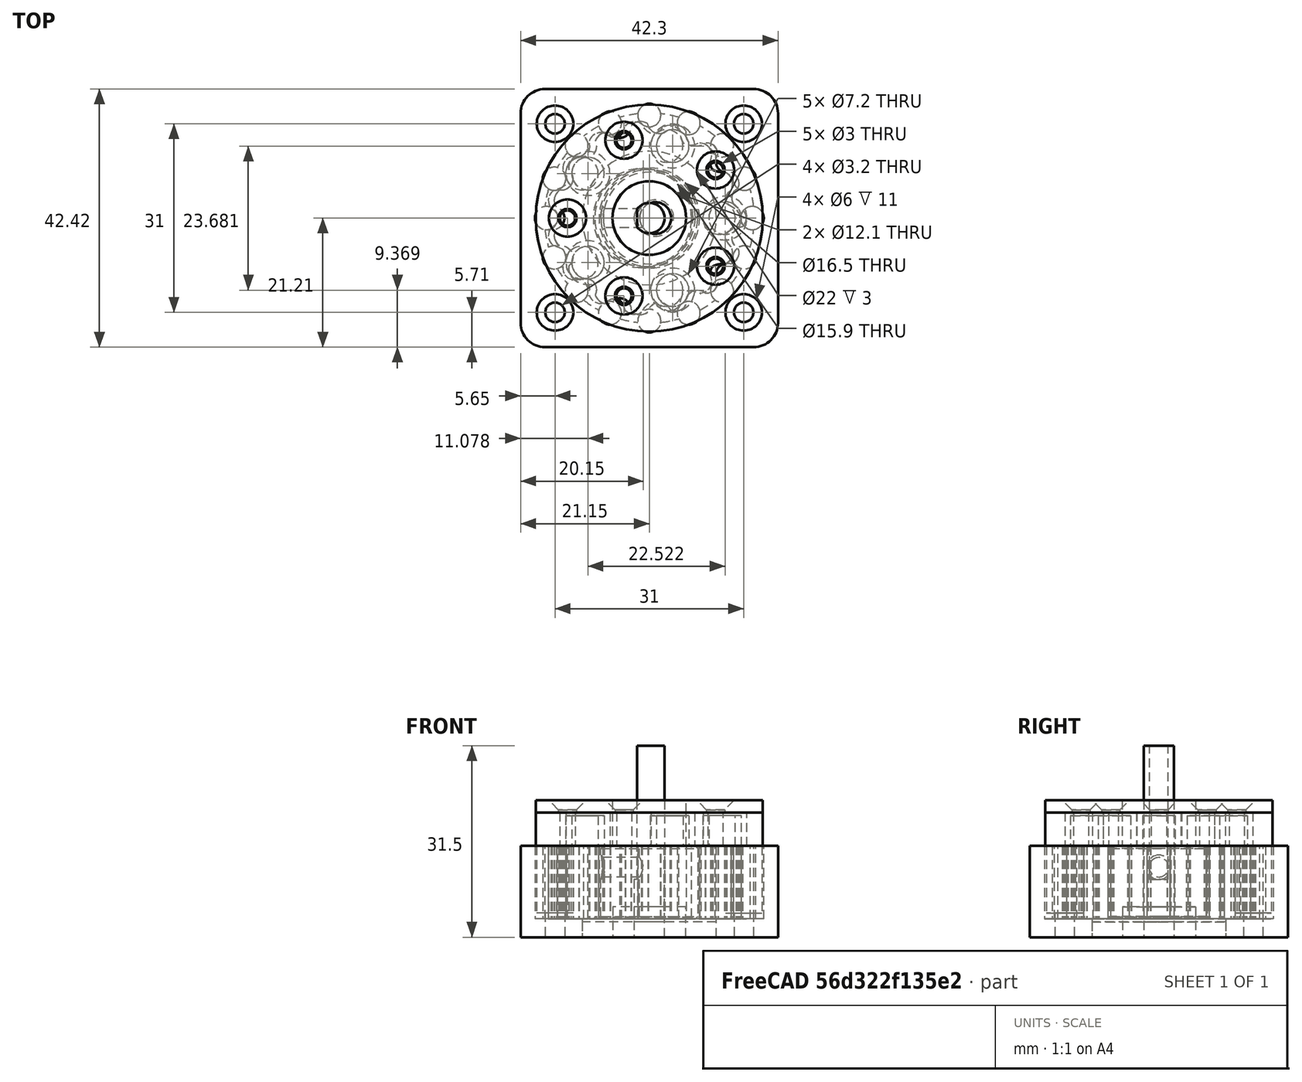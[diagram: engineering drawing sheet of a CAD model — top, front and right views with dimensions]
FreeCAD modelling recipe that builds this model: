
FCSTD DOCUMENT  (FreeCAD 0.21R31391 (Git))
Label: GearboxCycloidal
License: All rights reserved
LicenseURL: http://en.wikipedia.org/wiki/All_rights_reserved
objects: Sketcher::SketchObject×16, PartDesign::Pad×10, PartDesign::Body×9, App::Part×9, PartDesign::PolarPattern×4, TechDraw::DrawViewDimension×4, PartDesign::Pocket×3, PartDesign::FeaturePython×3, PartDesign::Hole×2, PartDesign::Mirrored×2, PartDesign::Chamfer×2, TechDraw::DrawViewPart×2, Spreadsheet::Sheet×1, PartDesign::Boolean×1, PartDesign::MultiTransform×1, Part::Feature×1, TechDraw::DrawSVGTemplate×1, TechDraw::DrawPage×1
note: 71 computed .brp shape members not serialized (recipe doc carries the construction recipe); baked Part::Feature solids carry a one-line shape summary decoded from their .brp

FEATURE [Spreadsheet::Sheet] Spreadsheet  label="SpreadSheet"
  cells = A2=Stepper; C2=Defaults; D2=enter negative numbers as =-0.5, not as -0.5; A3=StepperSize; B3(StepperSize)=42.3; A4=StepperShaftDiameter; B4(StepperShaftDiameter)=5; G4=Todo; A5=StepperShaftFlatLength; B5(StepperShaftFlatLength)=15; A6=StepperShaftFlatDepth; B6(StepperShaftFlatDepth)=0.5; A7=StepperShaftLength; B7(StepperShaftLength)=22; A8=StepperBoltHolediameter; B8(StepperBoltHolediameter)=3.2; A9=StepperRegisterDiameter; B9(StepperRegisterDiameter)=22; A10=StepperRegisterDepth; B10(StepperRegisterDepth)=2.5; A11=StepperBoltDistance; B11(StepperBoltDistance)=31; A12=StepperBodyCornerRadius; B12(StepperBodyCornerRadius)=4; A13=StepperShaftRotation; B13(StepperShaftRotation)=90; A15=GearBox; A16=GearBoxBaseThickness; B16(GearBoxBaseThickness)=0.5; D16=The gearbox bottom thickness above the the stepper register; A17=GearBoxBottomPosition; B17(GearBoxBottomPosition)==GearBoxBaseThickness + StepperRegisterDepth; D17=The heigth from the stepper flange to the gearbox bottom; A18=GearBoxGearPocketDiameter; B18(GearBoxGearPocketDiameter)=34.5; D18=The pocket for the cycloidal gear; A19=GearBoxRollerTopPosition; B19(GearBoxRollerTopPosition)==GearBoxBottomPosition + GearThickness; A20=GearBoxBoltHeadDiameter; B20(GearBoxBoltHeadDiameter)=6; A21=GearBoxBoltHeadDepth; B21(GearBoxBoltHeadDepth)==GearBoxRollerTopPosition - 4; A23=Cycloid Gear; A24=PinCircleRadiusCorrected; B24==PinCircleRadiusCorrection + PinCircleRadius; A25=PinCircleRadius; B25(PinCircleRadius)=16.9; C25=17; D25=The radius of the outside rollers; A26=PinCircleRadiusCorrection; B26(PinCircleRadiusCorrection)==-0.09; C26==-0.05; D26=3D printing correction for gear disk only, must be0 or lager than 0.1, otherwise error in gear calculation; A27=GearHoleRadius; B27(GearHoleRadius)=8; D27=The radius of the eccenter hole; A28=GearHoleRadiusCorrection; B28(GearHoleRadiusCorrection)==-0.05; D28=3D printing correction for gear disk only; A29=Eccentricity; B29(Eccentricity)=1; C29=1; D29=eccentricity of the eccenter; A30=GearThickness; B30(GearThickness)=12; C30=11; A31=RollerRotation; B31(RollerRotation)=0; C31=36; D31=To prevent the screw hole in the roller; A32=RollerDiameter; B32(RollerDiameter)=3.8; C32=5; A33=TeethNumber; B33(TeethNumber)=15; C33=10; D33=The number of teeth of the gear, defines the reduction; A35=GearCamDiameter; B35(GearCamDiameter)=5; D35=Diameter of the cam (shaft) to drive the shaft.; A36=GearCamDiameterCorrection; B36(GearCamDiameterCorrection)=0.35; A37=GearCamRadius; B37(GearCamRadius)==(GearHoleRadius + PinCircleRadius) / 2; C37=12.5; D37=The radius at witch the cams are placed; A38=GearCamThickness; B38(GearCamThickness)=5; C38=5; D38=The higth of the gear cams; A39=GearCamCount; B39(GearCamCount)=5; C39=5; D39=The number of gear cams; A40=SegementCount; B40(SegementCount)=16; C40=80; D40=High values are more precise. At higher roller counts, this results in errors; A42=Ecccenter; A43=EccenterOuterDiameter; B43(EccenterOuterDiameter)==GearHoleRadius * 2; C43=16; D43=The outer diameter of the eccenter; A44=EccenterOuterDiameterCorrection; B44(EccenterOuterDiameterCorrection)==0 - 0.1; C44=-0,1; D44=Correction for 3D print; A45=EccenterShaftHoleDiameter; B45(EccenterShaftHoleDiameter)==StepperShaftDiameter; C45=5; D45=The hole for the stepper shaft; A46=EccenterShaftHoleDiameterCorrection; B46(EccenterShaftHoleDiameterCorrection)=0.2; C46=0.2; D46=Correction for 3D print; A47=EccenterScrewHoleHeight; B47(EccenterScrewHoleHeight)=8.5; C47=8.5; D47=The position of the scres must be at the flat portion of the shaft; A48=EccenterScrewHoleDiameter; B48(EccenterScrewHoleDiameter)=3.2; C48=M4  3.2 mm; D48=The hole to tap the thread ; A49=EccenterRotation; B49(EccenterRotation)=90; C49=90; D49=To position the eccenter visual, just cosmetic ; A50=EccenterHeigth; B50(EccenterHeigth)==GearThickness; D50=The heigth of the eccenter; A52=OutputShaft; A53=OutputShaftDiameter; B53(OutputShaftDiameter)==StepperSize - 5; A54=OutputShaftThickNess; B54(OutputShaftThickNess)==GearCamThickness + 0.5; A55=PillarDiameterCorrection; B55(PillarDiameterCorrection)=-0.2; A56=OutputShaftCamHoleDiameter; B56(OutputShaftCamHoleDiameter)==GearCamDiameter + Eccentricity * 2; A57=OutputShaftCamHoleDiameterCorection; B57(OutputShaftCamHoleDiameterCorection)=0.2; A58=OutputShaftBoltDistance; B58(OutputShaftBoltDistance)==GearCamRadius + GearCamDiameter - 4; A59=OutputShaftBoltThreadDiameter; B59(OutputShaftBoltThreadDiameter)=2.5; A60=OutputShaftBoltDiameter; B60(OutputShaftBoltDiameter)=3; A61=OutputShaftTopPosition; B61(OutputShaftTopPosition)==GearBoxRollerTopPosition + OutputShaftThickNess; A62=OutputShaftHoleRotation; B62(OutputShaftHoleRotation)==90 - 360 / B53; A63=OutputShaftBearingOuterDiameterCorrection; B63(OutputShaftBearingOuterDiameterCorrection)=0.1; D63=Correction for 3D print; A65=GearMountingPlate; A66=GearMountingPlateThickness; B66(GearMountingPlateThickness)=2; A67=GearMountingPlateTopPosition; B67(GearMountingPlateTopPosition)==OutputShaftTopPosition + GearMountingPlateThickness; A68=GearMountingPlateDiameter; B68(GearMountingPlateDiameter)==OutputShaftDiameter; A69=GearMountingPlateBearingOuterDiameterCorrection; B69(GearMountingPlateBearingOuterDiameterCorrection)==OutputShaftBearingOuterDiameterCorrection; C69=0.1; D69=Correction for 3D print; A71=OutputGear; A72=OutputGearThickness; B72(OutputGearThickness)=6; A73=OutputGearTeeth; B73(OutputGearTeeth)=17; A74=OutputGearTopPosition; B74(OutputGearTopPosition)==OutputShaftTopPosition + OutputGearThickness; A75=OutputGearBearingPocketDepth; B75(OutputGearBearingPocketDepth)==BearingThickness - GearMountingPlateThickness; A76=OutputGearBearingOuterDiameterCorrection; B76(OutputGearBearingOuterDiameterCorrection)==OutputShaftBearingOuterDiameterCorrection; C76=0.1; D76=correction for 3D print; A78=Bearing; A79=BearingOuterDiameter; B79(BearingOuterDiameter)=12; A80=BearingInnerDiameter; B80(BearingInnerDiameter)=5; A81=BearingThickness; B81(BearingThickness)=5; A82=BearingTotalLength; B82==OutputGearTopPosition - GearBoxRollerTopPosition
FEATURE [Sketcher::SketchObject] Sketch026
  FullyConstrained = false
  MapMode = 5
  Support = -> [XY_Plane020]
  expr: Constraints[23] = Spreadsheet.StepperBodyCornerRadius
  expr: Constraints[27] = Spreadsheet.StepperRegisterDiameter
  expr: Constraints[5] = Spreadsheet.StepperSize
  sketch-geometry (13):
    g0: Circle CenterX=0 CenterY=0 CenterZ=0 NormalX=0 NormalY=0 NormalZ=1 AngleXU=0 Radius=11
    g1: LineSegment StartX=-17.15 StartY=21.2137 StartZ=0 EndX=17.15 EndY=21.2137 EndZ=0
    g2: LineSegment StartX=21.15 StartY=17.2137 StartZ=0 EndX=21.15 EndY=-17.2137 EndZ=0
    g3: LineSegment StartX=17.15 StartY=-21.2137 StartZ=0 EndX=-17.15 EndY=-21.2137 EndZ=0
    g4: LineSegment StartX=-21.15 StartY=-17.2137 StartZ=0 EndX=-21.15 EndY=17.2137 EndZ=0
    g5: ArcOfCircle CenterX=-17.15 CenterY=17.2137 CenterZ=0 NormalX=0 NormalY=0 NormalZ=1 AngleXU=0 Radius=4 StartAngle=1.5708 EndAngle=3.14159
    g6: GeomPoint X=-21.15 Y=21.2137 Z=0
    g7: ArcOfCircle CenterX=17.15 CenterY=17.2137 CenterZ=0 NormalX=0 NormalY=0 NormalZ=1 AngleXU=0 Radius=4 StartAngle=-9e-16 EndAngle=1.5708
    g8: GeomPoint X=21.15 Y=21.2137 Z=0
    g9: ArcOfCircle CenterX=-17.15 CenterY=-17.2137 CenterZ=0 NormalX=0 NormalY=0 NormalZ=1 AngleXU=0 Radius=4 StartAngle=3.14159 EndAngle=4.71239
    g10: GeomPoint X=-21.15 Y=-21.2137 Z=0
    g11: ArcOfCircle CenterX=17.15 CenterY=-17.2137 CenterZ=0 NormalX=0 NormalY=0 NormalZ=1 AngleXU=0 Radius=4 StartAngle=4.71239 EndAngle=6.28319
    g12: GeomPoint X=21.15 Y=-21.2137 Z=0
  constraints (28):
    c: Coincident(g0,g-1)
    c: Horizontal(g1)
    c: Horizontal(g3)
    c: Vertical(g2)
    c: Vertical(g4)
    c: DistanceX(g6,g8) = 42.3
    c: Symmetric(g10,g8,g0)
    c: PointOnObject(g6,g1)
    c: PointOnObject(g6,g4)
    c: Tangent(g1,g5) = 1.5708
    c: Tangent(g4,g5) = 1.5708
    c: PointOnObject(g8,g1)
    c: PointOnObject(g8,g2)
    c: Tangent(g1,g7) = 1.5708
    c: Tangent(g2,g7) = 1.5708
    c: PointOnObject(g10,g4)
    c: PointOnObject(g10,g3)
    c: Tangent(g4,g9) = 1.5708
    c: Tangent(g3,g9) = 1.5708
    c: PointOnObject(g12,g3)
    c: PointOnObject(g12,g2)
    c: Tangent(g3,g11) = 1.5708
    c: Tangent(g2,g11) = 1.5708
    c: Radius(g5) = 4
    c: Equal(g5,g7)
    c: Equal(g7,g11)
    c: Equal(g11,g9)
    c: Diameter(g0) = 22
FEATURE [PartDesign::Pad] Pad005
  Direction = (0,0,1)
  Length = 15
  Length2 = 10
  Profile = -> Sketch026
  ReferenceAxis = -> Sketch026 [N_Axis]
  Type = 0
  expr: Length = Spreadsheet.GearBoxRollerTopPosition
FEATURE [Sketcher::SketchObject] Sketch028
  FullyConstrained = true
  MapMode = 11
  Placement = pos=(0,0,15) rot=(0,0,1;1.5708rad)
  Support = -> [Pad005]
  expr: Constraints[1] = Spreadsheet.GearBoxGearPocketDiameter
  sketch-geometry (1):
    g0: Circle CenterX=0 CenterY=0 CenterZ=0 NormalX=0 NormalY=0 NormalZ=1 AngleXU=0 Radius=17.25
  constraints (2):
    c: Coincident(g0,g-1)
    c: Diameter(g0) = 34.5
FEATURE [PartDesign::Pocket] Pocket007
  BaseFeature = -> Pad005
  Direction = (0,0,-1)
  Length = 12
  Length2 = 5
  Profile = -> Sketch028
  ReferenceAxis = -> Sketch028 [N_Axis]
  Type = 0
  expr: Length = Spreadsheet.GearThickness
FEATURE [PartDesign::FeaturePython] hypocycloidgear003  label="HypoCycloidGearRollers"  # WARN: FeaturePython — macro-defined, semantics opaque (R4)
  AttacherType = Attacher::AttachEngine3D
  Placement = pos=(0,0,9) rot=(0,0,1;0rad)
  center_pins = true
  disk_height = 11.9
  eccentricity = 1
  hole_radius = 8
  pin_circle_radius = 16.9
  pin_height = 12
  pressure_angle_lim = 50
  pressure_angle_offset = 0.01
  roller_diameter = 3.8
  segment_count = 16
  show_disk0 = false
  show_disk1 = false
  show_pins = true
  teeth_number = 15
  version = 0.0.3
  expr: .Placement.Base.z = Spreadsheet.GearBoxBottomPosition + Spreadsheet.GearThickness / 2
  expr: .Placement.Rotation.Angle = Spreadsheet.RollerRotation
  expr: disk_height = Spreadsheet.GearThickness - 0.1
  expr: eccentricity = Spreadsheet.Eccentricity
  expr: hole_radius = Spreadsheet.GearHoleRadius
  expr: pin_circle_radius = Spreadsheet.PinCircleRadius
  expr: pin_height = Spreadsheet.GearThickness
  expr: roller_diameter = Spreadsheet.RollerDiameter
  expr: segment_count = Spreadsheet.SegementCount
  expr: teeth_number = Spreadsheet.TeethNumber
FEATURE [PartDesign::Body] Body006  label="HypoCycloidGearRollersBody"
  Group = -> [hypocycloidgear003]
  Origin = -> Origin021
  Tip = -> hypocycloidgear003
FEATURE [PartDesign::Boolean] Boolean
  BaseFeature = -> Pocket007
  Group = -> [Body006]
  Type = 0
FEATURE [Sketcher::SketchObject] Sketch029
  FullyConstrained = false
  MapMode = 5
  Placement = pos=(0,0,15) rot=(0,0,1;0rad)
  Support = -> [Boolean]
  expr: Constraints[10] = Spreadsheet.StepperBoltDistance
  expr: Constraints[11] = Spreadsheet.StepperBoltHolediameter
  sketch-geometry (5):
    g0: Circle CenterX=-15.5 CenterY=15.5 CenterZ=0 NormalX=0 NormalY=0 NormalZ=1 AngleXU=0 Radius=1.6
    g1: LineSegment StartX=-15.5 StartY=15.5 StartZ=0 EndX=15.5 EndY=15.5 EndZ=0
    g2: LineSegment StartX=15.5 StartY=15.5 StartZ=0 EndX=15.5 EndY=-15.5 EndZ=0
    g3: LineSegment StartX=15.5 StartY=-15.5 StartZ=0 EndX=-15.5 EndY=-15.5 EndZ=0
    g4: LineSegment StartX=-15.5 StartY=-15.5 StartZ=0 EndX=-15.5 EndY=15.5 EndZ=0
  constraints (12):
    c: Coincident(g1,g2)
    c: Coincident(g2,g3)
    c: Coincident(g3,g4)
    c: Coincident(g4,g1)
    c: Horizontal(g1)
    c: Horizontal(g3)
    c: Vertical(g2)
    c: Vertical(g4)
    c: Equal(g4,g1)
    c: Symmetric(g3,g1,g-1)
    c: DistanceX(g1,g1) = 31
    c: Diameter(g0) = 3.2
FEATURE [PartDesign::Hole] Hole
  BaseFeature = -> Boolean
  CustomThreadClearance = 0
  Depth = 124.756
  DepthType = 1
  Diameter = 3.2
  DrillForDepth = false
  DrillPoint = 1
  DrillPointAngle = 118
  HoleCutCountersinkAngle = 90
  HoleCutCustomValues = false
  HoleCutDepth = 11
  HoleCutDiameter = 6
  HoleCutType = 1
  ModelThread = false
  Profile = -> Sketch029
  Tapered = false
  TaperedAngle = 90
  ThreadClass = 0
  ThreadDepth = 124.756
  ThreadDepthType = 0
  ThreadDirection = 0
  ThreadFit = 0
  ThreadSize = 0
  ThreadType = 0
  Threaded = false
  UseCustomThreadClearance = false
  expr: Diameter = Spreadsheet.StepperBoltHolediameter
  expr: HoleCutDepth = Spreadsheet.GearBoxBoltHeadDepth
  expr: HoleCutDiameter = Spreadsheet.GearBoxBoltHeadDiameter
FEATURE [PartDesign::Mirrored] Mirrored
  MirrorPlane = -> Sketch029 [V_Axis]
FEATURE [PartDesign::Mirrored] Mirrored001
  MirrorPlane = -> XZ_Plane020
FEATURE [PartDesign::MultiTransform] MultiTransform
  BaseFeature = -> Hole
  Originals = -> [Hole]
  Transformations = -> [Mirrored,Mirrored001]
FEATURE [PartDesign::Body] Body005  label="NemaBaseBody"
  Group = -> [Sketch026,Pad005,Sketch028,Pocket007,Boolean,Sketch029,Hole,MultiTransform,Mirrored,Mirrored001]
  Origin = -> Origin020
  Tip = -> MultiTransform
FEATURE [App::Part] Part005  label="NemaBase"
  Group = -> [Body005]
  Origin = -> Origin019
FEATURE [PartDesign::FeaturePython] hypocycloidgear004  label="HypoCycloidGearDisk001"  # WARN: FeaturePython — macro-defined, semantics opaque (R4)
  AttacherType = Attacher::AttachEngine3D
  Placement = pos=(1,0,3) rot=(0,0,1;0rad)
  center_pins = true
  disk_height = 12
  eccentricity = 1
  hole_radius = 7.95
  pin_circle_radius = 16.81
  pin_height = 12
  pressure_angle_lim = 50
  pressure_angle_offset = 0.01
  roller_diameter = 3.8
  segment_count = 16
  show_disk0 = true
  show_disk1 = false
  show_pins = false
  teeth_number = 15
  version = 0.0.3
  expr: .Placement.Base.x = Spreadsheet.Eccentricity
  expr: .Placement.Base.z = Spreadsheet.GearBoxBottomPosition
  expr: .Placement.Rotation.Angle = Spreadsheet.RollerRotation
  expr: disk_height = Spreadsheet.GearThickness
  expr: eccentricity = Spreadsheet.Eccentricity
  expr: hole_radius = Spreadsheet.GearHoleRadius + Spreadsheet.GearHoleRadiusCorrection
  expr: pin_circle_radius = Spreadsheet.PinCircleRadius + Spreadsheet.PinCircleRadiusCorrection
  expr: pin_height = Spreadsheet.GearThickness
  expr: roller_diameter = Spreadsheet.RollerDiameter
  expr: segment_count = Spreadsheet.SegementCount
  expr: teeth_number = Spreadsheet.TeethNumber
FEATURE [Sketcher::SketchObject] Sketch035
  FullyConstrained = true
  MapMode = 5
  Support = -> [XY_Plane030]
  expr: Constraints[1] = Spreadsheet.StepperRegisterDiameter
  sketch-geometry (1):
    g0: Circle CenterX=0 CenterY=0 CenterZ=0 NormalX=0 NormalY=0 NormalZ=1 AngleXU=0 Radius=11
  constraints (2):
    c: Coincident(g0,g-1)
    c: Diameter(g0) = 22
FEATURE [PartDesign::Pad] Pad
  Direction = (0,0,1)
  Length = 2.5
  Length2 = 10
  Profile = -> Sketch035
  ReferenceAxis = -> Sketch035 [N_Axis]
  Type = 0
  expr: Length = Spreadsheet.StepperRegisterDepth
FEATURE [Sketcher::SketchObject] Sketch036
  FullyConstrained = true
  MapMode = 5
  Placement = pos=(0,0,2.5) rot=(0,0,1;0rad)
  Support = -> [Pad]
  expr: Constraints[1] = Spreadsheet.StepperShaftDiameter
  sketch-geometry (1):
    g0: Circle CenterX=0 CenterY=0 CenterZ=0 NormalX=0 NormalY=0 NormalZ=1 AngleXU=0 Radius=2.5
  constraints (2):
    c: Coincident(g0,g-1)
    c: Diameter(g0) = 5
FEATURE [PartDesign::Pad] Pad008
  BaseFeature = -> Pad
  Direction = (0,0,1)
  Length = 7
  Length2 = 10
  Profile = -> Sketch036
  ReferenceAxis = -> Sketch036 [N_Axis]
  Type = 0
  expr: Length = Spreadsheet.StepperShaftLength - Spreadsheet.StepperShaftFlatLength
FEATURE [Sketcher::SketchObject] Sketch037
  AttachmentOffset = pos=(0,0,0) rot=(0,0,1;1.5708rad)
  FullyConstrained = false
  MapMode = 5
  Placement = pos=(0,0,9.5) rot=(0,0,1;1.5708rad)
  Support = -> [Pad008]
  expr: .AttachmentOffset.Rotation.Angle = Spreadsheet.StepperShaftRotation
  expr: Constraints[2] = Spreadsheet.StepperShaftDiameter
  sketch-geometry (2):
    g0: ArcOfCircle CenterX=0 CenterY=0 CenterZ=0 NormalX=0 NormalY=0 NormalZ=1 AngleXU=0 Radius=2.5 StartAngle=2.2143 EndAngle=7.21048
    g1: LineSegment StartX=-1.5 StartY=2 StartZ=0 EndX=1.5 EndY=2 EndZ=0
  constraints (5):
    c: Coincident(g0,g-1)
    c: Horizontal(g1)
    c: Diameter(g0) = 5
    c: Coincident(g0,g1)
    c: Coincident(g0,g1)
FEATURE [PartDesign::Pad] Pad009
  BaseFeature = -> Pad008
  Direction = (0,0,1)
  Length = 22
  Length2 = 10
  Profile = -> Sketch037
  ReferenceAxis = -> Sketch037 [N_Axis]
  Type = 0
  expr: Length = Spreadsheet.StepperShaftLength
FEATURE [PartDesign::Body] Body008  label="ShaftBody"
  Group = -> [Sketch035,Pad,Sketch036,Pad008,Sketch037,Pad009]
  Origin = -> Origin030
  Tip = -> Pad009
FEATURE [App::Part] Part007  label="Shaft"
  Group = -> [Body008]
  Origin = -> Origin029
FEATURE [Sketcher::SketchObject] Sketch038
  FullyConstrained = true
  MapMode = 5
  Support = -> [XY_Plane032]
  expr: Constraints[1] = Spreadsheet.OutputShaftDiameter
  expr: Constraints[3] = Spreadsheet.BearingOuterDiameter + Spreadsheet.OutputShaftBearingOuterDiameterCorrection
  sketch-geometry (2):
    g0: Circle CenterX=0 CenterY=0 CenterZ=0 NormalX=0 NormalY=0 NormalZ=1 AngleXU=0 Radius=18.65
    g1: Circle CenterX=0 CenterY=0 CenterZ=0 NormalX=0 NormalY=0 NormalZ=1 AngleXU=0 Radius=6.05
  constraints (4):
    c: Coincident(g0,g-1)
    c: Diameter(g0) = 37.3
    c: Coincident(g1,g0)
    c: Diameter(g1) = 12.1
FEATURE [PartDesign::Pad] Pad010
  Direction = (0,0,1)
  Length = 5.5
  Length2 = 10
  Profile = -> Sketch038
  ReferenceAxis = -> Sketch038 [N_Axis]
  Type = 0
  expr: Length = Spreadsheet.OutputShaftThickNess
FEATURE [Sketcher::SketchObject] Sketch039
  FullyConstrained = true
  MapMode = 5
  expr: Constraints[0] = Spreadsheet.OutputShaftCamHoleDiameter + Spreadsheet.OutputShaftCamHoleDiameterCorection
  expr: Constraints[2] = Spreadsheet.GearCamRadius
  expr: Constraints[5] = 360 / Spreadsheet.GearCamCount / 2
  expr: Constraints[6] = Spreadsheet.OutputShaftBoltDistance
  expr: Constraints[7] = Spreadsheet.OutputShaftBoltThreadDiameter
  sketch-geometry (3):
    g0: Circle CenterX=12.45 CenterY=0 CenterZ=0 NormalX=0 NormalY=0 NormalZ=1 AngleXU=0 Radius=3.6
    g1: Circle CenterX=10.8813 CenterY=7.90571 CenterZ=0 NormalX=0 NormalY=0 NormalZ=1 AngleXU=0 Radius=1.25
    g2: LineSegment StartX=10.8813 StartY=7.90571 StartZ=0 EndX=0 EndY=0 EndZ=0
  constraints (8):
    c: Diameter(g0) = 7.2
    c: PointOnObject(g0,g-1)
    c: DistanceX(g-1,g0) = 12.45
    c: Coincident(g2,g1)
    c: Coincident(g2,g-1)
    c: Angle(g-1,g2) = 0.628319
    c: Distance(g2,g1) = 13.45
    c: Diameter(g1) = 2.5
FEATURE [PartDesign::Pocket] Pocket008
  BaseFeature = -> Pad010
  Direction = (0,0,-1)
  Length = 5
  Length2 = 5
  Profile = -> Sketch039
  ReferenceAxis = -> Sketch039 [N_Axis]
  Reversed = true
  Type = 1
FEATURE [PartDesign::PolarPattern] PolarPattern001
  Angle = 360
  Axis = -> Z_Axis032
  BaseFeature = -> Pocket008
  Occurrences = 5
  Originals = -> [Pocket008]
  expr: Occurrences = Spreadsheet.GearCamCount
FEATURE [PartDesign::Body] Body009  label="OutputShaftBody"
  Group = -> [Sketch038,Pad010,Sketch039,Pocket008,PolarPattern001]
  Origin = -> Origin032
  Placement = pos=(0,0,15) rot=(0,0,1;0rad)
  Tip = -> PolarPattern001
  expr: .Placement.Base.z = Spreadsheet.GearBoxRollerTopPosition
FEATURE [App::Part] Part008  label="OutputShaft"
  Group = -> [Body009]
  Origin = -> Origin031
FEATURE [Sketcher::SketchObject] Sketch041
  FullyConstrained = true
  MapMode = 5
  Support = -> [XY_Plane034]
  expr: Constraints[2] = Spreadsheet.BearingInnerDiameter
  expr: Constraints[3] = Spreadsheet.BearingOuterDiameter
  sketch-geometry (2):
    g0: Circle CenterX=0 CenterY=0 CenterZ=0 NormalX=0 NormalY=0 NormalZ=1 AngleXU=0 Radius=2.5
    g1: Circle CenterX=0 CenterY=0 CenterZ=0 NormalX=0 NormalY=0 NormalZ=1 AngleXU=0 Radius=6
  constraints (4):
    c: Coincident(g0,g-1)
    c: Coincident(g1,g0)
    c: Diameter(g0) = 5
    c: Diameter(g1) = 12
FEATURE [PartDesign::Pad] Pad011
  Direction = (0,0,1)
  Length = 5
  Length2 = 10
  Profile = -> Sketch041
  ReferenceAxis = -> Sketch041 [N_Axis]
  Type = 0
  expr: Length = Spreadsheet.BearingThickness
FEATURE [PartDesign::Body] Body010  label="Bearing11x5x5Body"
  Group = -> [Sketch041,Pad011]
  Origin = -> Origin034
  Tip = -> Pad011
FEATURE [App::Part] Part009  label="Bearing11x5x5"
  Group = -> [Body010]
  Origin = -> Origin033
  Placement = pos=(0,0,15) rot=(0,0,1;0rad)
  expr: .Placement.Base.z = Spreadsheet.GearBoxRollerTopPosition
FEATURE [Sketcher::SketchObject] Sketch046
  AttachmentOffset = pos=(0,0,20.5) rot=(0,0,1;0rad)
  FullyConstrained = true
  MapMode = 5
  Placement = pos=(0,0,20.5) rot=(0,0,1;0rad)
  Support = -> [XY_Plane041]
  expr: .AttachmentOffset.Base.z = Spreadsheet.OutputShaftTopPosition
  expr: Constraints[1] = Spreadsheet.GearMountingPlateDiameter
  expr: Constraints[3] = Spreadsheet.BearingOuterDiameter + Spreadsheet.GearMountingPlateBearingOuterDiameterCorrection
  sketch-geometry (2):
    g0: Circle CenterX=0 CenterY=0 CenterZ=0 NormalX=0 NormalY=0 NormalZ=1 AngleXU=0 Radius=18.65
    g1: Circle CenterX=0 CenterY=0 CenterZ=0 NormalX=0 NormalY=0 NormalZ=1 AngleXU=0 Radius=6.05
  constraints (4):
    c: Coincident(g0,g-1)
    c: Diameter(g0) = 37.3
    c: Coincident(g1,g0)
    c: Diameter(g1) = 12.1
FEATURE [PartDesign::Pad] Pad013
  Direction = (0,0,1)
  Length = 2
  Length2 = 10
  Profile = -> Sketch046
  ReferenceAxis = -> Sketch046 [N_Axis]
  Type = 0
  expr: Length = Spreadsheet.GearMountingPlateThickness
FEATURE [Sketcher::SketchObject] Sketch047
  FullyConstrained = true
  MapMode = 5
  Placement = pos=(0,0,22.5) rot=(0,0,1;0rad)
  Support = -> [Pad013]
  expr: Constraints[0] = Spreadsheet.OutputShaftBoltDistance
  expr: Constraints[1] = Spreadsheet.OutputShaftBoltThreadDiameter
  expr: Constraints[4] = 360 / Spreadsheet.GearCamCount / 2
  sketch-geometry (2):
    g0: Circle CenterX=10.8813 CenterY=7.90571 CenterZ=0 NormalX=0 NormalY=0 NormalZ=1 AngleXU=0 Radius=1.25
    g1: LineSegment StartX=10.8813 StartY=7.90571 StartZ=0 EndX=0 EndY=0 EndZ=0
  constraints (5):
    c: Distance(g-1,g0) = 13.45
    c: Diameter(g0) = 2.5
    c: Coincident(g1,g0)
    c: Coincident(g1,g-1)
    c: Angle(g-1,g1) = 0.628319
FEATURE [PartDesign::Hole] Hole001
  BaseFeature = -> Pad013
  CustomThreadClearance = 0
  Depth = 118.051
  DepthType = 1
  Diameter = 3
  DrillForDepth = false
  DrillPoint = 1
  DrillPointAngle = 118
  HoleCutCountersinkAngle = 90
  HoleCutCustomValues = false
  HoleCutDepth = 0
  HoleCutDiameter = 6.1
  HoleCutType = 2
  ModelThread = false
  Profile = -> Sketch047
  Tapered = false
  TaperedAngle = 90
  ThreadClass = 0
  ThreadDepth = 118.051
  ThreadDepthType = 0
  ThreadDirection = 0
  ThreadFit = 0
  ThreadSize = 0
  ThreadType = 0
  Threaded = false
  UseCustomThreadClearance = false
  expr: Diameter = Spreadsheet.OutputShaftBoltDiameter
FEATURE [PartDesign::PolarPattern] PolarPattern002
  Angle = 360
  Axis = -> Sketch047 [N_Axis]
  BaseFeature = -> Hole001
  Occurrences = 5
  Originals = -> [Hole001]
  expr: Occurrences = Spreadsheet.GearCamCount
FEATURE [PartDesign::Body] Body013  label="GearMountingPlateBody"
  Group = -> [Pad013,Sketch046,Sketch047,Hole001,PolarPattern002]
  Origin = -> Origin041
  Tip = -> PolarPattern002
FEATURE [App::Part] Part011  label="GearMountingPlate"
  Group = -> [Body013]
  Origin = -> Origin040
FEATURE [Sketcher::SketchObject] Sketch
  AttachmentOffset = pos=(0,0,15) rot=(0,0,1;0rad)
  FullyConstrained = true
  MapMode = 5
  Placement = pos=(0,0,15) rot=(0,0,1;0rad)
  Support = -> [XY_Plane042]
  expr: .AttachmentOffset.Base.z = Spreadsheet.GearBoxRollerTopPosition
  expr: Constraints[0] = Spreadsheet.GearCamDiameter + Spreadsheet.GearCamDiameterCorrection
  expr: Constraints[2] = Spreadsheet.GearCamRadius
  expr: Constraints[4] = Spreadsheet.GearHoleRadius * 2
  sketch-geometry (2):
    g0: Circle CenterX=12.45 CenterY=0 CenterZ=0 NormalX=0 NormalY=0 NormalZ=1 AngleXU=0 Radius=2.675
    g1: Circle CenterX=0 CenterY=0 CenterZ=0 NormalX=0 NormalY=0 NormalZ=1 AngleXU=0 Radius=8
  constraints (5):
    c: Diameter(g0) = 5.35
    c: PointOnObject(g0,g-1)
    c: DistanceX(g-1,g0) = 12.45
    c: Coincident(g1,g-1)
    c: Diameter(g1) = 16
FEATURE [PartDesign::Pad] Pad014
  BaseFeature = -> hypocycloidgear004
  Direction = (0,0,1)
  Length = 5
  Length2 = 10
  Placement = pos=(1,0,3) rot=(0,0,1;0rad)
  Profile = -> Sketch
  ReferenceAxis = -> Sketch [N_Axis]
  Type = 0
  expr: Length = Spreadsheet.GearCamThickness
FEATURE [PartDesign::PolarPattern] PolarPattern003
  Angle = 360
  Axis = -> Sketch [N_Axis]
  BaseFeature = -> Pad014
  Occurrences = 5
  Originals = -> [Pad014]
  Placement = pos=(1,0,3) rot=(0,0,1;0rad)
  expr: Occurrences = Spreadsheet.GearCamCount
FEATURE [PartDesign::Body] Body014  label="HypoCycloidalGearBody"
  Group = -> [hypocycloidgear004,Sketch,Pad014,PolarPattern003]
  Origin = -> Origin042
  Tip = -> PolarPattern003
FEATURE [Sketcher::SketchObject] Sketch048  label="Sketch for checking alignment"
  AttachmentOffset = pos=(0,0,12) rot=(0,0,1;0rad)
  FullyConstrained = false
  MapMode = 5
  Placement = pos=(0,0,12) rot=(0,0,1;0rad)
  Support = -> [XY_Plane047]
  expr: .AttachmentOffset.Base.z = Spreadsheet.GearThickness
  expr: Constraints[1] = Spreadsheet.EccenterOuterDiameter
  sketch-geometry (3):
    g0: Circle CenterX=0 CenterY=0 CenterZ=0 NormalX=0 NormalY=0 NormalZ=1 AngleXU=0 Radius=8
    g1: Circle CenterX=0 CenterY=0 CenterZ=0 NormalX=0 NormalY=0 NormalZ=1 AngleXU=0 Radius=2.54745
    g2: Circle CenterX=0 CenterY=0 CenterZ=0 NormalX=0 NormalY=0 NormalZ=1 AngleXU=0 Radius=10.5035
  constraints (4):
    c: Coincident(g0,g-1)
    c: Diameter(g0) = 16
    c: Coincident(g1,g0)
    c: Coincident(g2,g0)
FEATURE [Sketcher::SketchObject] Sketch051
  AttachmentOffset = pos=(0,0,0) rot=(0,0,1;1.5708rad)
  FullyConstrained = true
  MapMode = 5
  Placement = pos=(0,0,0) rot=(0,0,1;1.5708rad)
  Support = -> [XY_Plane043]
  expr: .AttachmentOffset.Rotation.Angle = Spreadsheet.EccenterRotation
  expr: Constraints[2] = Spreadsheet.EccenterOuterDiameter + Spreadsheet.EccenterOuterDiameterCorrection
  expr: Constraints[3] = Spreadsheet.EccenterShaftHoleDiameter + Spreadsheet.EccenterShaftHoleDiameterCorrection
  expr: Constraints[4] = Spreadsheet.Eccentricity
  sketch-geometry (2):
    g0: Circle CenterX=0 CenterY=0 CenterZ=0 NormalX=0 NormalY=0 NormalZ=1 AngleXU=0 Radius=7.95
    g1: Circle CenterX=-1 CenterY=0 CenterZ=0 NormalX=0 NormalY=0 NormalZ=1 AngleXU=0 Radius=2.6
  constraints (5):
    c: Coincident(g0,g-1)
    c: PointOnObject(g1,g-1)
    c: Diameter(g0) = 15.9
    c: Diameter(g1) = 5.2
    c: DistanceX(g1,g0) = 1
FEATURE [PartDesign::Pad] Pad016
  Direction = (0,0,1)
  Length = 12
  Length2 = 10
  Profile = -> Sketch051
  ReferenceAxis = -> Sketch051 [N_Axis]
  Type = 0
  expr: Length = Spreadsheet.GearThickness
FEATURE [Sketcher::SketchObject] Sketch052
  AttachmentOffset = pos=(0,0,-8) rot=(0,0,1;0rad)
  FullyConstrained = true
  MapMode = 5
  Placement = pos=(0,8,1.8e-15) rot=(1,0,0;1.5708rad)
  Support = -> [XZ_Plane043]
  expr: .AttachmentOffset.Base.z = -Spreadsheet.EccenterOuterDiameter / 2
  expr: Constraints[1] = Spreadsheet.EccenterScrewHoleDiameter
  expr: Constraints[2] = Spreadsheet.EccenterScrewHoleHeight
  sketch-geometry (1):
    g0: Circle CenterX=0 CenterY=8.5 CenterZ=0 NormalX=0 NormalY=0 NormalZ=1 AngleXU=0 Radius=1.6
  constraints (3):
    c: PointOnObject(g0,g-2)
    c: Diameter(g0) = 3.2
    c: DistanceY(g-1,g0) = 8.5
FEATURE [PartDesign::Pocket] Pocket
  BaseFeature = -> Pad016
  Direction = (0,1,2e-16)
  Length = 8
  Length2 = 5
  Profile = -> Sketch052
  ReferenceAxis = -> Sketch052 [N_Axis]
  Reversed = true
  Type = 0
  expr: Length = Spreadsheet.EccenterOuterDiameter / 2
FEATURE [PartDesign::Chamfer] Chamfer
  Angle = 45
  Base = -> Pocket [Face1,Edge8]
  BaseFeature = -> Pocket
  ChamferType = 0
  FlipDirection = false
  Size = 0.4
  Size2 = 1
  SupportTransform = false
  UseAllEdges = false
FEATURE [PartDesign::Body] Body  label="EccenterBody"
  Group = -> [Sketch051,Pad016,Sketch052,Pocket,Chamfer]
  Origin = -> Origin043
  Placement = pos=(0,0,3) rot=(0,0,1;1.5708rad)
  Tip = -> Chamfer
  expr: .Placement.Base.z = Spreadsheet.GearBoxBottomPosition
  expr: .Placement.Rotation.Angle = Spreadsheet.EccenterRotation
FEATURE [Part::Feature] Part__Feature  label="GearMountingPlateBody001"
  shape: bbox 37.3 x 37.3 x 2 mm, 14 faces (baked)
FEATURE [App::Part] GearMountingPlate  label="GearMountingPlate2"
  Group = -> [Part__Feature]
  Origin = -> Origin044
FEATURE [TechDraw::DrawSVGTemplate] Template
  EditableTexts = Designed_by_Name=Designed by Name; Drawing_number=Drawing number; FC-Date=Date; FC-SC=Scale; FC-SH=Sheet; FC-Title=Title; Subtitle=Subtitle; Weight=Weight
  Height = 210
  Orientation = 1
  Width = 297
FEATURE [PartDesign::FeaturePython] hypocycloidgear005  # WARN: FeaturePython — macro-defined, semantics opaque (R4)
  AttacherType = Attacher::AttachEngine3D
  center_pins = true
  disk_height = 12
  eccentricity = 1
  hole_radius = 7.95
  pin_circle_radius = 16.81
  pin_height = 12
  pressure_angle_lim = 50
  pressure_angle_offset = 0.01
  roller_diameter = 3.8
  segment_count = 16
  show_disk0 = true
  show_disk1 = false
  show_pins = false
  teeth_number = 15
  version = 0.0.3
  expr: disk_height = Spreadsheet.GearThickness
  expr: eccentricity = Spreadsheet.Eccentricity
  expr: hole_radius = Spreadsheet.GearHoleRadius + Spreadsheet.GearHoleRadiusCorrection
  expr: pin_circle_radius = Spreadsheet.PinCircleRadius + Spreadsheet.PinCircleRadiusCorrection
  expr: pin_height = Spreadsheet.GearThickness
  expr: roller_diameter = Spreadsheet.RollerDiameter
  expr: segment_count = Spreadsheet.SegementCount
  expr: teeth_number = Spreadsheet.TeethNumber
FEATURE [Sketcher::SketchObject] Sketch054
  AttachmentOffset = pos=(-1,0,11.95) rot=(0,0,1;0rad)
  FullyConstrained = true
  MapMode = 2
  Placement = pos=(-1,0,11.95) rot=(0,0,1;0rad)
  Support = -> [hypocycloidgear005]
  expr: Constraints[2] = Spreadsheet.GearCamDiameter + Spreadsheet.GearCamDiameterCorrection
  sketch-geometry (1):
    g0: Circle CenterX=12.45 CenterY=0 CenterZ=0 NormalX=0 NormalY=0 NormalZ=1 AngleXU=0 Radius=2.675
  constraints (3):
    c: PointOnObject(g0,g-1)
    c: DistanceX(g-1,g0) = 12.45
    c: Diameter(g0) = 5.35
FEATURE [PartDesign::Pad] Pad017
  BaseFeature = -> hypocycloidgear005
  Direction = (0,0,1)
  Length = 5
  Length2 = 10
  Profile = -> Sketch054
  ReferenceAxis = -> Sketch054 [N_Axis]
  Type = 0
FEATURE [PartDesign::PolarPattern] PolarPattern
  Angle = 360
  Axis = -> Sketch054 [N_Axis]
  BaseFeature = -> Pad017
  Occurrences = 5
  Originals = -> [Pad017]
FEATURE [PartDesign::Chamfer] Chamfer001
  Angle = 45
  Base = -> PolarPattern [Edge59]
  BaseFeature = -> PolarPattern
  ChamferType = 0
  FlipDirection = false
  Size = 0.25
  Size2 = 1
  SupportTransform = false
  UseAllEdges = false
FEATURE [PartDesign::Body] Body016
  Group = -> [hypocycloidgear005,Sketch054,Pad017,PolarPattern,Chamfer001]
  Origin = -> Origin001
  Placement = pos=(0,0,3) rot=(0,0,1;0rad)
  Tip = -> Chamfer001
  expr: .Placement.Base.z = Spreadsheet.GearBoxBottomPosition
FEATURE [App::Part] Part013  label="HypoCycloidGearDisk Use this for printing"
  Group = -> [Body016,Sketch048]
  Origin = -> Origin047
FEATURE [App::Part] Part  label="HypoCycloidGearDisk"
  Group = -> [Body014]
  Origin = -> Origin
  Placement = pos=(-1,0,0) rot=(0,0,1;0rad)
  expr: .Placement.Base.x = -Spreadsheet.Eccentricity
FEATURE [TechDraw::DrawViewPart] View  label="HypoCycloidGearDisk TV"
  CoarseView = false
  Direction = (0,0,1)
  Focus = 100
  HardHidden = false
  IsoCount = 0
  IsoHidden = false
  IsoVisible = false
  LockPosition = false
  Perspective = false
  Rotation = 0
  ScaleType = 0
  SeamHidden = false
  SeamVisible = true
  SmoothHidden = false
  SmoothVisible = true
  Source = -> [Part]
  X = 86.5611
  XDirection = (1,0,0)
  Y = 152.38
FEATURE [TechDraw::DrawViewDimension] Dimension003
  AngleOverride = false
  Arbitrary = false
  ArbitraryTolerances = false
  EqualTolerance = true
  ExtensionAngle = 0
  FormatSpec = ⌀%.2f
  FormatSpecOverTolerance = %+.2f
  FormatSpecUnderTolerance = %+.2f
  Inverted = false
  LineAngle = 0
  LockPosition = false
  MeasureType = 1
  OverTolerance = 0
  References2D = -> [View]
  Rotation = 0
  ScaleType = 0
  TheoreticalExact = false
  Type = 5
  UnderTolerance = 0
  X = -22.2579
  Y = 26.8238
FEATURE [App::Part] Part014  label="Eccenter"
  Group = -> [Body]
  Origin = -> Origin048
FEATURE [TechDraw::DrawViewPart] View001  label="HypoCycloidGearDisk Use this for printing001"
  CoarseView = false
  Direction = (0,0,1)
  Focus = 100
  HardHidden = false
  IsoCount = 0
  IsoHidden = false
  IsoVisible = false
  LockPosition = false
  Perspective = false
  Rotation = 0
  ScaleType = 0
  SeamHidden = false
  SeamVisible = true
  SmoothHidden = false
  SmoothVisible = true
  Source = -> [Part013]
  X = 88.2538
  XDirection = (1,0,0)
  Y = 87.3724
FEATURE [TechDraw::DrawViewDimension] Dimension004
  AngleOverride = false
  Arbitrary = false
  ArbitraryTolerances = false
  EqualTolerance = true
  ExtensionAngle = 0
  FormatSpec = ⌀%.2f
  FormatSpecOverTolerance = %+.2f
  FormatSpecUnderTolerance = %+.2f
  Inverted = false
  LineAngle = 0
  LockPosition = false
  MeasureType = 1
  OverTolerance = 0
  References2D = -> [View001]
  Rotation = 0
  ScaleType = 0
  TheoreticalExact = false
  Type = 5
  UnderTolerance = 0
  X = 25.6172
  Y = 27.4843
FEATURE [TechDraw::DrawViewDimension] Dimension005
  AngleOverride = false
  Arbitrary = false
  ArbitraryTolerances = false
  EqualTolerance = true
  ExtensionAngle = 0
  FormatSpec = ⌀%.2f
  FormatSpecOverTolerance = %+.2f
  FormatSpecUnderTolerance = %+.2f
  Inverted = false
  LineAngle = 0
  LockPosition = false
  MeasureType = 1
  OverTolerance = 0
  References2D = -> [View001]
  Rotation = 0
  ScaleType = 0
  TheoreticalExact = false
  Type = 5
  UnderTolerance = 0
  X = 32.4445
  Y = 12.9496
FEATURE [TechDraw::DrawViewDimension] Dimension
  AngleOverride = false
  Arbitrary = false
  ArbitraryTolerances = false
  EqualTolerance = true
  ExtensionAngle = 0
  FormatSpec = ⌀%.2f
  FormatSpecOverTolerance = %+.2f
  FormatSpecUnderTolerance = %+.2f
  Inverted = false
  LineAngle = 0
  LockPosition = false
  MeasureType = 1
  OverTolerance = 0
  References2D = -> [View]
  Rotation = 0
  ScaleType = 0
  TheoreticalExact = false
  Type = 5
  UnderTolerance = 0
  X = -31.5255
  Y = 9.3409
FEATURE [TechDraw::DrawPage] Page  label="Drawings"
  KeepUpdated = true
  NextBalloonIndex = 1
  ProjectionType = 0
  Template = -> Template
  Views = -> [View,Dimension003,View001,Dimension004,Dimension005,Dimension]
